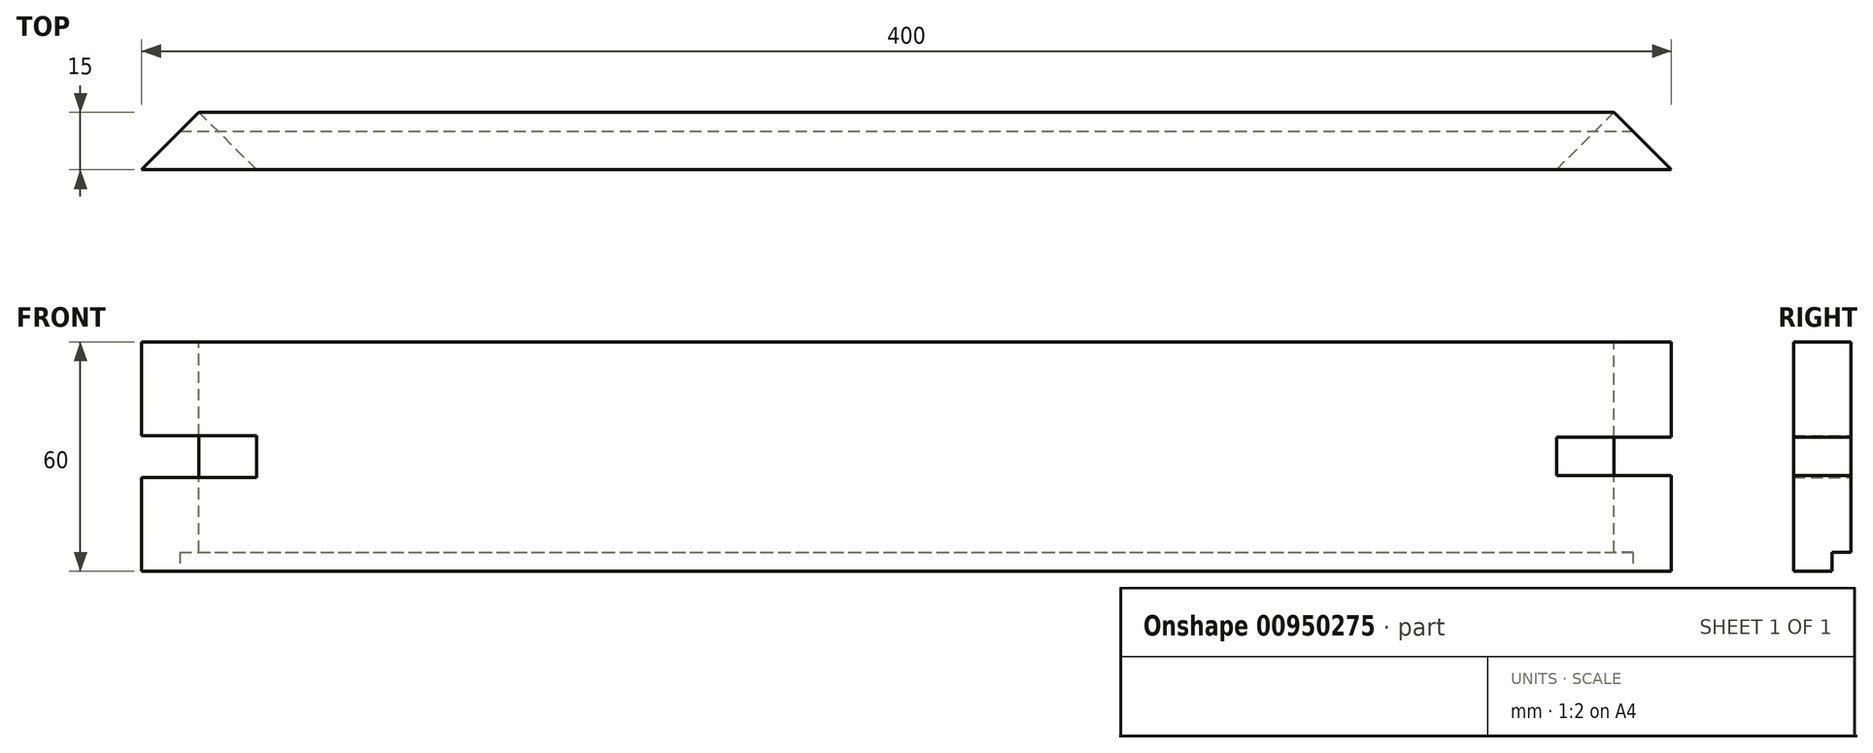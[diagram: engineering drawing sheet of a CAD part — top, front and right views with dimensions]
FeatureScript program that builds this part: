
annotation { "Feature Type Name" : "Feature", "Feature Type Description" : "" }
export const myFeature = defineFeature(function(context is Context, id is Id, definition is map)
    precondition{}
    {
        {
            var Q0;
            Q0=qCreatedBy(makeId("Front.planeOp"),FACE);
            var sketch = newSketch(context, id + "F0", { "sketchPlane" : qUnion([Q0])});
            skLineSegment(sketch, "E0.bottom", {"start": v(200, -30) * mm, "end": v(-200, -30) * mm});
            skLineSegment(sketch, "E0.top", {"start": v(200, 30) * mm, "end": v(-200, 30) * mm});
            skLineSegment(sketch, "E0.left", {"start": v(200, -30) * mm, "end": v(200, 30) * mm});
            skLineSegment(sketch, "E0.right", {"start": v(-200, -30) * mm, "end": v(-200, 30) * mm});
            skPoint(sketch, "E0.middle", {"position": v(0, 0) * mm});
            skSolve(sketch);
        }
        {
            var Q0;
            Q0=makeQuery(id+"F0.imprint","IMPRINT",FACE,{"disambiguationData":[TD([[makeQuery(id+"F0.imprint","IMPRINT",EDGE,{"derivedFrom":sQuery(id+"F0.wireOp",EDGE,"E0.bottom")}),-1.0]])]});
            extrude(context, id + "F1", {"entities" : qUnion([Q0]), "endBound" : BoundingType.SYMMETRIC, "depth" : 15 * mm, "offsetDistance" : 25 * mm});
        }
        {
            var Q0;
            Q0=makeQuery(id+"F1.opExtrude","SWEPT_FACE",FACE,{"disambiguationData":[OSD([sQuery(id+"F0.wireOp",EDGE,"E0.top")])]});
            var sketch = newSketch(context, id + "F2", { "sketchPlane" : qUnion([Q0])});
            skLineSegment(sketch, "E1", {"start": v(200, -7.5) * mm, "end": v(200, 7.5) * mm});
            skLineSegment(sketch, "E2", {"start": v(200, 7.5) * mm, "end": v(185, 7.5) * mm});
            skLineSegment(sketch, "E3", {"start": v(185, 7.5) * mm, "end": v(200, -7.5) * mm});
            skLineSegment(sketch, "E4", {"start": v(-200, -7.5) * mm, "end": v(-200, 7.5) * mm});
            skLineSegment(sketch, "E5", {"start": v(-200, 7.5) * mm, "end": v(-185, 7.5) * mm});
            skLineSegment(sketch, "E6", {"start": v(-185, 7.5) * mm, "end": v(-200, -7.5) * mm});
            skSolve(sketch);
        }
        {
            var Q0;
            Q0=makeQuery(id+"F2.imprint","IMPRINT",FACE,{"disambiguationData":[TD([[makeQuery(id+"F2.imprint","IMPRINT",EDGE,{"derivedFrom":sQuery(id+"F2.wireOp",EDGE,"E4")}),-1.0]])]});
            var Q1;
            Q1=makeQuery(id+"F2.imprint","IMPRINT",FACE,{"disambiguationData":[TD([[makeQuery(id+"F2.imprint","IMPRINT",EDGE,{"derivedFrom":sQuery(id+"F2.wireOp",EDGE,"E1")}),1.0]])]});
            extrude(context, id + "F3", {"entities" : qUnion([Q0, Q1]), "operationType" : NewBodyOperationType.REMOVE, "oppositeDirection" : true, "depth" : 60 * mm, "offsetDistance" : 25 * mm});
        }
        {
            var Q0;
            Q0=makeQuery(id+"F3.boolean.opBoolean","COPY",FACE,{"derivedFrom":makeQuery(id+"F3.opExtrude","SWEPT_FACE",FACE,{"disambiguationData":[OSD([sQuery(id+"F2.wireOp",EDGE,"E3")])]})});
            var sketch = newSketch(context, id + "F4", { "sketchPlane" : qUnion([Q0])});
            skLineSegment(sketch, "E7.bottom", {"start": v(-125.51, -5) * mm, "end": v(-146.72, -5) * mm});
            skLineSegment(sketch, "E7.top", {"start": v(-125.51, 5) * mm, "end": v(-146.72, 5) * mm});
            skLineSegment(sketch, "E7.left", {"start": v(-125.51, -5) * mm, "end": v(-125.51, 5) * mm});
            skLineSegment(sketch, "E7.right", {"start": v(-146.72, -5) * mm, "end": v(-146.72, 5) * mm});
            skPoint(sketch, "E7.middle", {"position": v(-136.12, 0) * mm});
            skSolve(sketch);
        }
        {
            var Q0;
            Q0=makeQuery(id+"F4.imprint","IMPRINT",FACE,{"disambiguationData":[TD([[makeQuery(id+"F4.imprint","IMPRINT",EDGE,{"derivedFrom":sQuery(id+"F4.wireOp",EDGE,"E7.bottom")}),-1.0]])]});
            extrude(context, id + "F5", {"entities" : qUnion([Q0]), "operationType" : NewBodyOperationType.REMOVE, "oppositeDirection" : true, "depth" : 25 * mm, "offsetDistance" : 25 * mm});
        }
        {
            var Q0;
            Q0=makeQuery(id+"F3.boolean.opBoolean","COPY",FACE,{"derivedFrom":makeQuery(id+"F3.opExtrude","SWEPT_FACE",FACE,{"disambiguationData":[OSD([sQuery(id+"F2.wireOp",EDGE,"E6")])]})});
            var sketch = newSketch(context, id + "F6", { "sketchPlane" : qUnion([Q0])});
            skLineSegment(sketch, "E8.bottom", {"start": v(146.72, -5.45) * mm, "end": v(125.51, -5.45) * mm});
            skLineSegment(sketch, "E8.top", {"start": v(146.72, 5.45) * mm, "end": v(125.51, 5.45) * mm});
            skLineSegment(sketch, "E8.left", {"start": v(146.72, -5.45) * mm, "end": v(146.72, 5.45) * mm});
            skLineSegment(sketch, "E8.right", {"start": v(125.51, -5.45) * mm, "end": v(125.51, 5.45) * mm});
            skPoint(sketch, "E8.middle", {"position": v(136.12, 0) * mm});
            skSolve(sketch);
        }
        {
            var Q0;
            Q0=makeQuery(id+"F6.imprint","IMPRINT",FACE,{"disambiguationData":[TD([[makeQuery(id+"F6.imprint","IMPRINT",EDGE,{"derivedFrom":sQuery(id+"F6.wireOp",EDGE,"E8.bottom")}),-1.0]])]});
            extrude(context, id + "F7", {"entities" : qUnion([Q0]), "operationType" : NewBodyOperationType.REMOVE, "oppositeDirection" : true, "depth" : 25 * mm, "offsetDistance" : 25 * mm});
        }
        {
            var Q0;
            Q0=qCreatedBy(makeId("Right.planeOp"),FACE);
            var sketch = newSketch(context, id + "F8", { "sketchPlane" : qUnion([Q0])});
            skLineSegment(sketch, "E9.bottom", {"start": v(7.5, -30) * mm, "end": v(2.5, -30) * mm});
            skLineSegment(sketch, "E9.top", {"start": v(7.5, -25) * mm, "end": v(2.5, -25) * mm});
            skLineSegment(sketch, "E9.left", {"start": v(7.5, -30) * mm, "end": v(7.5, -25) * mm});
            skLineSegment(sketch, "E9.right", {"start": v(2.5, -30) * mm, "end": v(2.5, -25) * mm});
            skSolve(sketch);
        }
        {
            var Q0;
            Q0=makeQuery(id+"F8.imprint","IMPRINT",FACE,{"disambiguationData":[TD([[makeQuery(id+"F8.imprint","IMPRINT",EDGE,{"derivedFrom":sQuery(id+"F8.wireOp",EDGE,"E9.bottom")}),-1.0]])]});
            extrude(context, id + "F9", {"entities" : qUnion([Q0]), "operationType" : NewBodyOperationType.REMOVE, "endBound" : BoundingType.SYMMETRIC, "oppositeDirection" : true, "depth" : 400 * mm, "offsetDistance" : 25 * mm});
        }
    });
